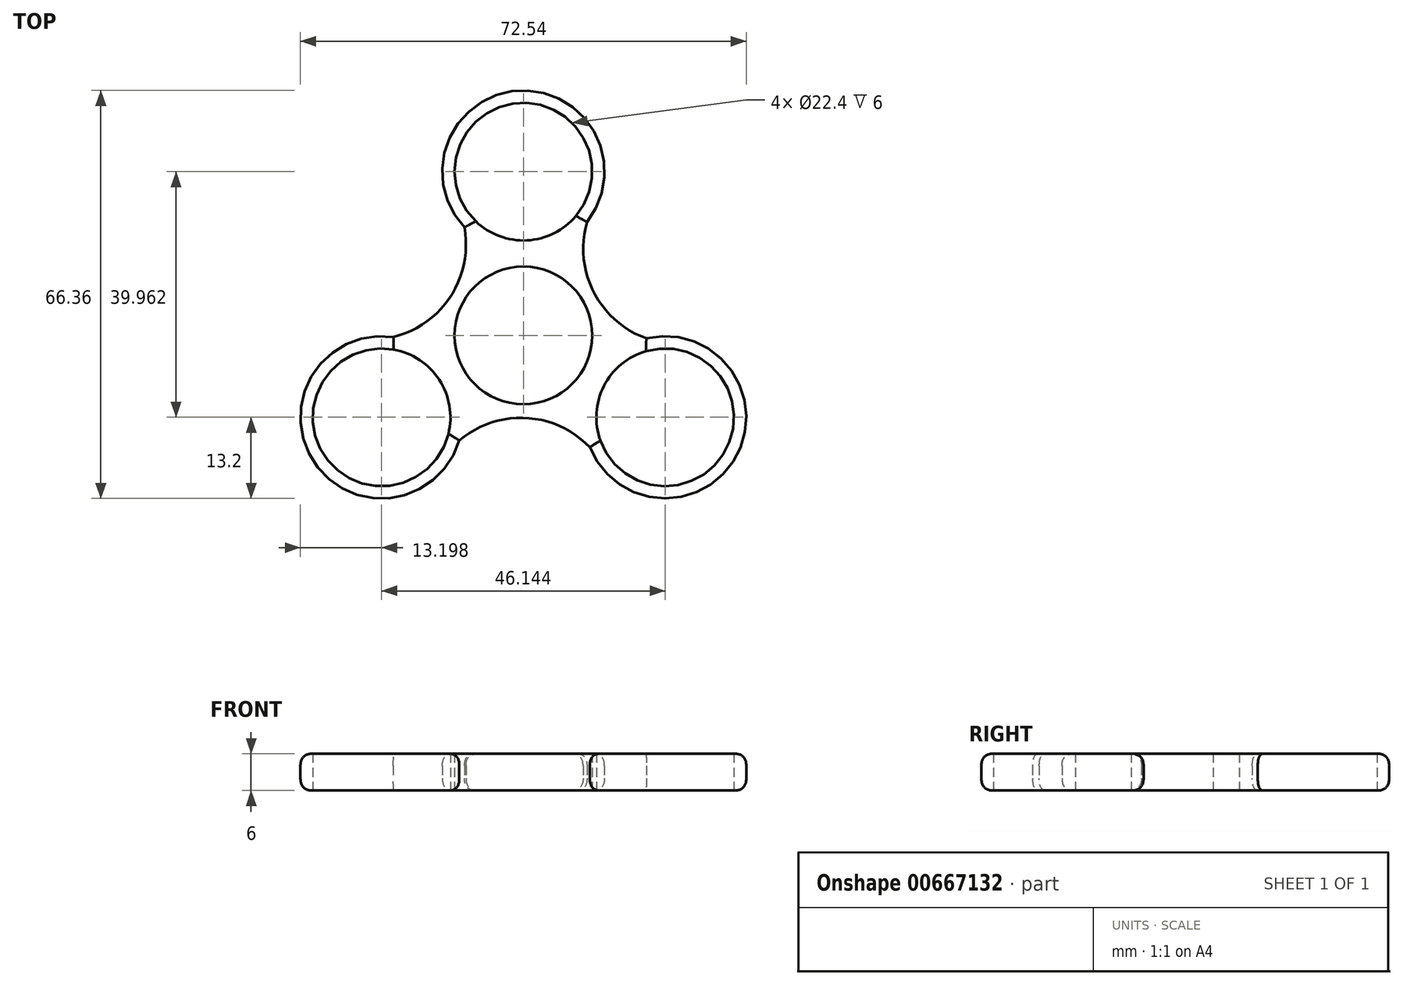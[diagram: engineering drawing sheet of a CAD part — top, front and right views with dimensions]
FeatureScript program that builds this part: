
annotation { "Feature Type Name" : "Feature", "Feature Type Description" : "" }
export const myFeature = defineFeature(function(context is Context, id is Id, definition is map)
    precondition{}
    {
        {
            var Q0;
            Q0=qCreatedBy(makeId("Top.planeOp"),FACE);
            var sketch = newSketch(context, id + "F0", { "sketchPlane" : qUnion([Q0])});
            skCircle(sketch, "E0", {"center": v(0, 0) * mm, "radius": 11.2 * mm});
            skCircle(sketch, "E1", {"center": v(0, 26.64) * mm, "radius": 11.2 * mm});
            skArc(sketch, "E2", {"start": v(10.36, 18.46) * mm, "mid": v(-0.58, 39.83) * mm, "end": v(-9.6, 17.58) * mm});
            skArc(sketch, "E3.1.0", {"start": v(-21.16, -0.26) * mm, "mid": v(-34.2, -20.42) * mm, "end": v(-10.42, -17.1) * mm});
            skCircle(sketch, "E3.1.1", {"center": v(-23.07, -13.32) * mm, "radius": 11.2 * mm});
            skArc(sketch, "E3.2.0", {"start": v(10.8, -18.2) * mm, "mid": v(34.78, -19.41) * mm, "end": v(20.02, -0.48) * mm});
            skCircle(sketch, "E3.2.1", {"center": v(23.07, -13.32) * mm, "radius": 11.2 * mm});
            skArc(sketch, "E4", {"start": v(10.36, 18.46) * mm, "mid": v(11.42, 7.07) * mm, "end": v(20.02, -0.48) * mm});
            skArc(sketch, "E5.1.0", {"start": v(-21.16, -0.26) * mm, "mid": v(-11.83, 6.36) * mm, "end": v(-9.6, 17.58) * mm});
            skArc(sketch, "E5.2.0", {"start": v(10.8, -18.2) * mm, "mid": v(0.4, -13.43) * mm, "end": v(-10.42, -17.1) * mm});
            skSolve(sketch);
        }
        {
            var Q0;
            Q0=makeQuery(id+"F0.imprint","IMPRINT",FACE,{"disambiguationData":[TD([[makeQuery(id+"F0.imprint","IMPRINT",EDGE,{"derivedFrom":sQuery(id+"F0.wireOp",EDGE,"E0")}),-1.0]])]});
            extrude(context, id + "F1", {"entities" : qUnion([Q0]), "depth" : 6 * mm, "offsetDistance" : 25 * mm});
        }
        {
            var Q0;
            Q0=makeQuery(id+"F1.opExtrude","CAP_EDGE",EDGE,{"disambiguationData":[OSD([sQuery(id+"F0.wireOp",EDGE,"E5.2.0")])],"isStart":false});
            var Q1;
            Q1=makeQuery(id+"F1.opExtrude","CAP_EDGE",EDGE,{"disambiguationData":[OSD([sQuery(id+"F0.wireOp",EDGE,"E5.2.0")])],"isStart":true});
            var Q2;
            Q2=makeQuery(id+"F1.opExtrude","CAP_EDGE",EDGE,{"disambiguationData":[OSD([sQuery(id+"F0.wireOp",EDGE,"E5.1.0")])],"isStart":false});
            var Q3;
            Q3=makeQuery(id+"F1.opExtrude","CAP_EDGE",EDGE,{"disambiguationData":[OSD([sQuery(id+"F0.wireOp",EDGE,"E5.1.0")])],"isStart":true});
            var Q4;
            Q4=makeQuery(id+"F1.opExtrude","CAP_EDGE",EDGE,{"disambiguationData":[OSD([sQuery(id+"F0.wireOp",EDGE,"E4")])],"isStart":true});
            var Q5;
            Q5=makeQuery(id+"F1.opExtrude","CAP_EDGE",EDGE,{"disambiguationData":[OSD([sQuery(id+"F0.wireOp",EDGE,"E4")])],"isStart":false});
            var Q6;
            Q6=makeQuery(id+"F1.opExtrude","CAP_EDGE",EDGE,{"disambiguationData":[OSD([sQuery(id+"F0.wireOp",EDGE,"E2")])],"isStart":false});
            var Q7;
            Q7=makeQuery(id+"F1.opExtrude","CAP_EDGE",EDGE,{"disambiguationData":[OSD([sQuery(id+"F0.wireOp",EDGE,"E2")])],"isStart":true});
            var Q8;
            Q8=makeQuery(id+"F1.opExtrude","CAP_EDGE",EDGE,{"disambiguationData":[OSD([sQuery(id+"F0.wireOp",EDGE,"E3.2.0")])],"isStart":true});
            var Q9;
            Q9=makeQuery(id+"F1.opExtrude","CAP_EDGE",EDGE,{"disambiguationData":[OSD([sQuery(id+"F0.wireOp",EDGE,"E3.2.0")])],"isStart":false});
            var Q10;
            Q10=makeQuery(id+"F1.opExtrude","CAP_EDGE",EDGE,{"disambiguationData":[OSD([sQuery(id+"F0.wireOp",EDGE,"E3.1.0")])],"isStart":false});
            var Q11;
            Q11=makeQuery(id+"F1.opExtrude","CAP_EDGE",EDGE,{"disambiguationData":[OSD([sQuery(id+"F0.wireOp",EDGE,"E3.1.0")])],"isStart":true});
            fillet(context, id + "F2", {"entities" : qUnion([Q0, Q1, Q2, Q3, Q4, Q5, Q6, Q7, Q8, Q9, Q10, Q11]), "radius" : 2 * mm, "tangentPropagation" : true, "rho" : 0.5, "crossSection" : FilletCrossSection.CONIC, "allowEdgeOverflow" : false});
        }
    });
